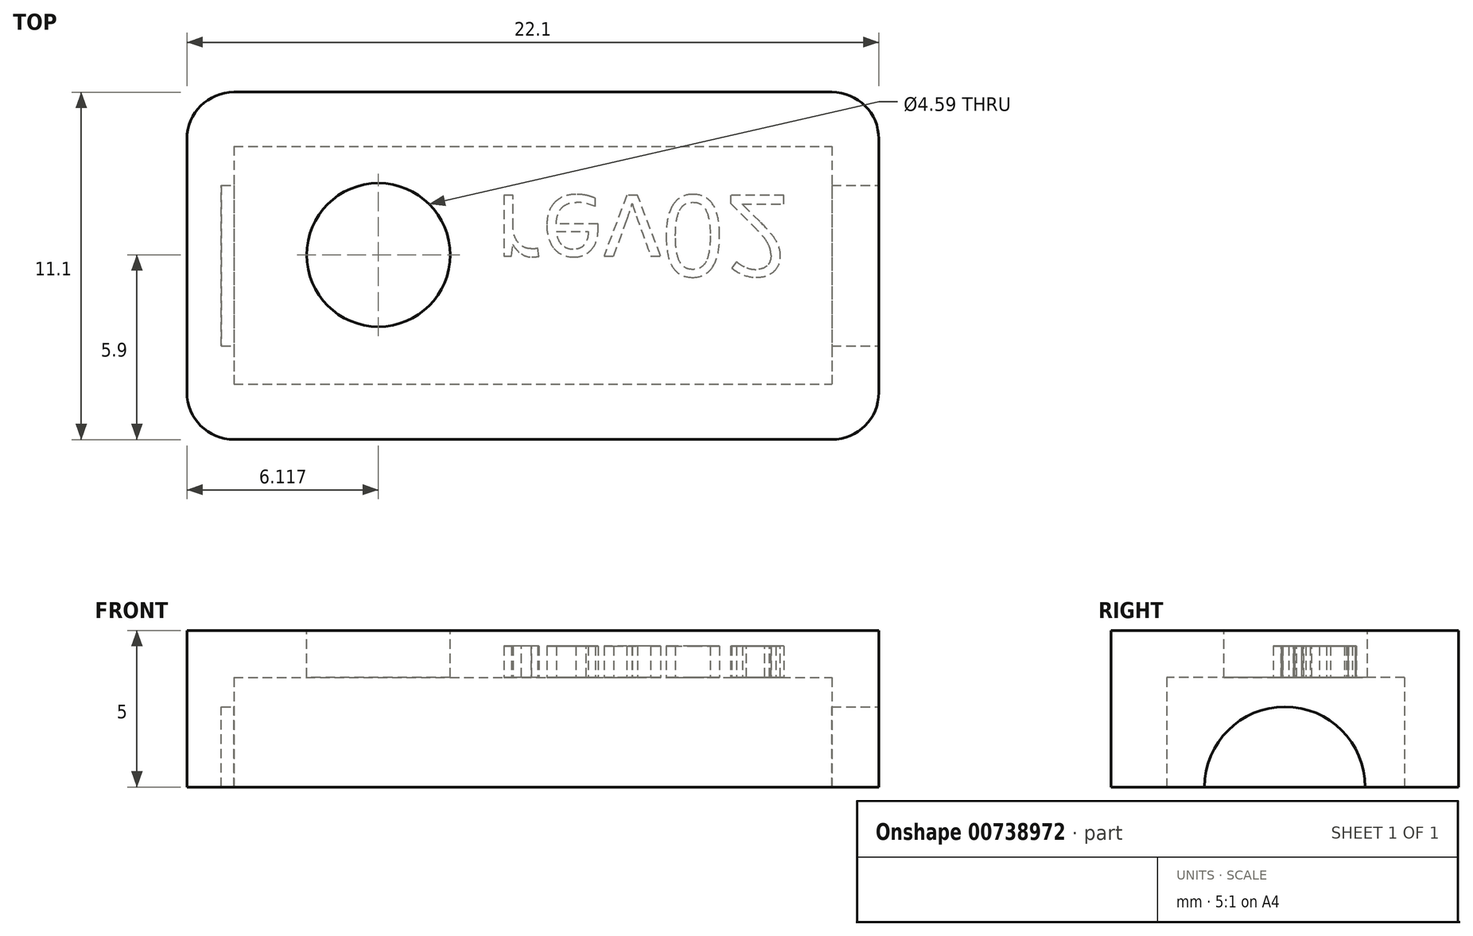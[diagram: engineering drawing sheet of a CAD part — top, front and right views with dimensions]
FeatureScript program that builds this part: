
annotation { "Feature Type Name" : "Feature", "Feature Type Description" : "" }
export const myFeature = defineFeature(function(context is Context, id is Id, definition is map)
    precondition{}
    {
        {
            var Q0;
            Q0=qCreatedBy(makeId("Top.planeOp"),FACE);
            var sketch = newSketch(context, id + "F0", { "sketchPlane" : qUnion([Q0])});
            skLineSegment(sketch, "E0.bottom", {"start": v(-7.6, 3.47) * mm, "end": v(11.5, 3.47) * mm});
            skLineSegment(sketch, "E0.top", {"start": v(-7.6, -4.13) * mm, "end": v(11.5, -4.13) * mm});
            skLineSegment(sketch, "E0.left", {"start": v(-7.6, 3.47) * mm, "end": v(-7.6, -4.13) * mm});
            skLineSegment(sketch, "E0.right", {"start": v(11.5, 3.47) * mm, "end": v(11.5, -4.13) * mm});
            skSolve(sketch);
        }
        {
            var Q0;
            Q0=qCreatedBy(makeId("Top.planeOp"),FACE);
            var sketch = newSketch(context, id + "F1", { "sketchPlane" : qUnion([Q0])});
            skLineSegment(sketch, "E1.bottom", {"start": v(-9.09, 5.2) * mm, "end": v(13.01, 5.2) * mm});
            skLineSegment(sketch, "E1.top", {"start": v(-9.09, -5.9) * mm, "end": v(13.01, -5.9) * mm});
            skLineSegment(sketch, "E1.left", {"start": v(-9.09, 5.2) * mm, "end": v(-9.09, -5.9) * mm});
            skLineSegment(sketch, "E1.right", {"start": v(13.01, 5.2) * mm, "end": v(13.01, -5.9) * mm});
            skSolve(sketch);
        }
        {
            var Q0;
            Q0 = qSketchRegion(id + "F1", true);
            extrude(context, id + "F2", {"entities" : qUnion([Q0]), "depth" : 5 * mm, "offsetDistance" : 25 * mm});
        }
        {
            var Q0;
            Q0 = qSketchRegion(id + "F0", true);
            extrude(context, id + "F3", {"entities" : qUnion([Q0]), "operationType" : NewBodyOperationType.REMOVE, "oppositeDirection" : true, "depth" : -3.5 * mm, "offsetDistance" : 25 * mm});
        }
        {
            var Q0;
            Q0=makeQuery(id+"F2.opExtrude","SWEPT_EDGE",EDGE,{"disambiguationData":[OSD([sQuery(id+"F1.wireOp",EDGE,"E1.bottom"),sQuery(id+"F1.wireOp",EDGE,"E1.left")])]});
            var Q1;
            Q1=makeQuery(id+"F2.opExtrude","SWEPT_EDGE",EDGE,{"disambiguationData":[OSD([sQuery(id+"F1.wireOp",EDGE,"E1.top"),sQuery(id+"F1.wireOp",EDGE,"E1.left")])]});
            var Q2;
            Q2=makeQuery(id+"F2.opExtrude","SWEPT_EDGE",EDGE,{"disambiguationData":[OSD([sQuery(id+"F1.wireOp",EDGE,"E1.bottom"),sQuery(id+"F1.wireOp",EDGE,"E1.right")])]});
            var Q3;
            Q3=makeQuery(id+"F2.opExtrude","SWEPT_EDGE",EDGE,{"disambiguationData":[OSD([sQuery(id+"F1.wireOp",EDGE,"E1.top"),sQuery(id+"F1.wireOp",EDGE,"E1.right")])]});
            fillet(context, id + "F4", {"entities" : qUnion([Q0, Q1, Q2, Q3]), "radius" : 1.5 * mm, "tangentPropagation" : true, "allowEdgeOverflow" : false});
        }
        {
            var Q0;
            Q0=makeQuery(id+"F2.opExtrude","CAP_FACE",FACE,{"disambiguationData":[OSD([sQuery(id+"F1.wireOp",EDGE,"E1.bottom"),sQuery(id+"F1.wireOp",EDGE,"E1.top"),sQuery(id+"F1.wireOp",EDGE,"E1.left"),sQuery(id+"F1.wireOp",EDGE,"E1.right")])],"isStart":false});
            var sketch = newSketch(context, id + "F5", { "sketchPlane" : qUnion([Q0])});
            skCircle(sketch, "E2", {"center": v(-2.97, 0) * mm, "radius": 2.3 * mm});
            skSolve(sketch);
        }
        {
            var Q0;
            Q0 = qSketchRegion(id + "F5", true);
            extrude(context, id + "F6", {"entities" : qUnion([Q0]), "operationType" : NewBodyOperationType.REMOVE, "oppositeDirection" : true, "depth" : 4 * mm, "offsetDistance" : 25 * mm});
        }
        {
            var Q0;
            Q0=makeQuery(id+"F2.opExtrude","SWEPT_FACE",FACE,{"disambiguationData":[OSD([sQuery(id+"F1.wireOp",EDGE,"E1.right")])]});
            var sketch = newSketch(context, id + "F7", { "sketchPlane" : qUnion([Q0])});
            skCircle(sketch, "E3", {"center": v(-0.35, 0) * mm, "radius": 2.56 * mm});
            skSolve(sketch);
        }
        {
            var Q0;
            Q0 = qSketchRegion(id + "F7", true);
            extrude(context, id + "F8", {"entities" : qUnion([Q0]), "operationType" : NewBodyOperationType.REMOVE, "oppositeDirection" : true, "depth" : 21 * mm, "offsetDistance" : 25 * mm});
        }
        {
            var Q0;
            Q0=makeQuery(id+"F3.boolean.opBoolean","COPY",FACE,{"derivedFrom":makeQuery(id+"F3.opExtrude","CAP_FACE",FACE,{"disambiguationData":[OSD([sQuery(id+"F0.wireOp",EDGE,"E0.bottom"),sQuery(id+"F0.wireOp",EDGE,"E0.top"),sQuery(id+"F0.wireOp",EDGE,"E0.left"),sQuery(id+"F0.wireOp",EDGE,"E0.right")])],"isStart":false})});
            var sketch = newSketch(context, id + "F9", { "sketchPlane" : qUnion([Q0])});
            skText(sketch, "E4", { "text": "rev02", "fontName": "OpenSans-Regular.ttf"});
            const initialGuessF9  = {"E4": [0.00073, -0.0019, 1, 0, 0.0026]};
            skSetInitialGuess(sketch, initialGuessF9);
            skSolve(sketch);
        }
        {
            var Q0;
            Q0 = qSketchRegion(id + "F9", true);
            extrude(context, id + "F10", {"entities" : qUnion([Q0]), "operationType" : NewBodyOperationType.REMOVE, "oppositeDirection" : true, "depth" : 1 * mm, "offsetDistance" : 25 * mm});
        }
    });
